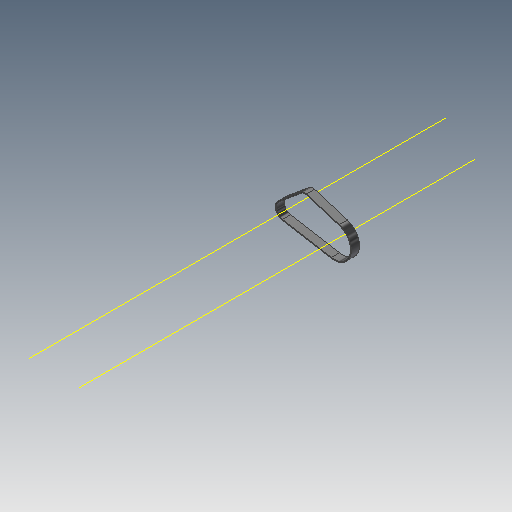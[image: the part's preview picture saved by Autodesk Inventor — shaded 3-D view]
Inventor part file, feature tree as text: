
AUTODESK INVENTOR PART (.ipt)
format: ipt  version: 2018 (Build 220112000, 112)  size: 109,056 bytes
history: native  units: mm (DEFAULTED — no unit token found)
features: other x5, plane x3, sketch x1, sweep x1
ambient origin geometry x8: Origin, YZ Plane, XZ Plane, XY Plane, X Axis, Y Axis, Z Axis, Center Point
bodies: Solid1 (feature_tree)
feature tree (10):
  sketch  "Sketch Path"  dims[d0=6.0mm d2=0.0mm d4=0.3mm d5=0.3mm d6=0.0mm d7=0.0mm d8=0.0mm d9=0.0mm d10=0.0mm d11=0.0mm d12=0.0mm d13=0.0mm]
  other  "Cross Section Plane"
  other  "Work Axis1"
  other  "Work Axis2"
  other  "Work Axis3"
  plane  "Work Plane2"
  plane  "Work Plane3"
  plane  "Work Plane4"
  sweep  "Belt"
  other  "Cross Section"
